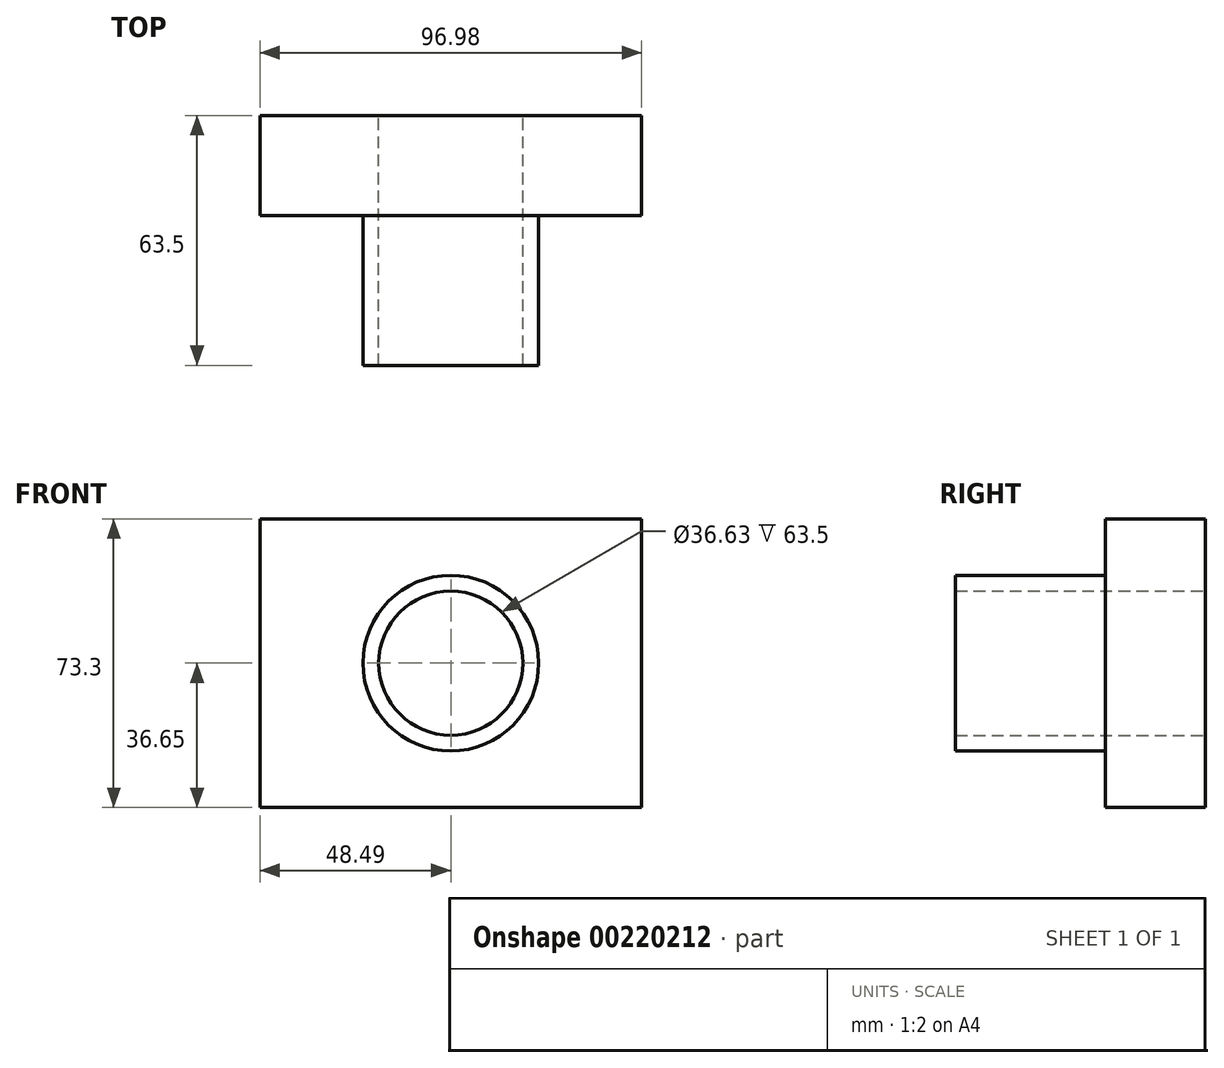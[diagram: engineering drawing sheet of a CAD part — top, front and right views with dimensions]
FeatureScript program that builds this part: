
annotation { "Feature Type Name" : "Feature", "Feature Type Description" : "" }
export const myFeature = defineFeature(function(context is Context, id is Id, definition is map)
    precondition{}
    {
        {
            var Q0;
            Q0=qCreatedBy(makeId("Front.planeOp"),FACE);
            var sketch = newSketch(context, id + "F0", { "sketchPlane" : qUnion([Q0])});
            skLineSegment(sketch, "E0.bottom", {"start": v(-48.5, 36.65) * mm, "end": v(48.5, 36.65) * mm});
            skLineSegment(sketch, "E0.top", {"start": v(-48.5, -36.65) * mm, "end": v(48.5, -36.65) * mm});
            skLineSegment(sketch, "E0.left", {"start": v(-48.5, 36.65) * mm, "end": v(-48.5, -36.65) * mm});
            skLineSegment(sketch, "E0.right", {"start": v(48.5, 36.65) * mm, "end": v(48.5, -36.65) * mm});
            skPoint(sketch, "E0.middle", {"position": v(0, 0) * mm});
            skSolve(sketch);
        }
        {
            var Q0;
            Q0=makeQuery(id+"F0.imprint","IMPRINT",FACE,{"disambiguationData":[TD([[makeQuery(id+"F0.imprint","IMPRINT",EDGE,{"derivedFrom":sQuery(id+"F0.wireOp",EDGE,"E0.bottom")}),-1.0]])]});
            var sketch = newSketch(context, id + "F1", { "sketchPlane" : qUnion([Q0])});
            skCircle(sketch, "E1", {"center": v(0, 0) * mm, "radius": 22.33 * mm});
            skSolve(sketch);
        }
        {
            var Q0;
            Q0=makeQuery(id+"F1.imprint","IMPRINT",FACE,{"disambiguationData":[TD([[makeQuery(id+"F1.imprint","IMPRINT",EDGE,{"derivedFrom":sQuery(id+"F1.wireOp",EDGE,"E1")}),1.0]])]});
            var sketch = newSketch(context, id + "F2", { "sketchPlane" : qUnion([Q0])});
            skCircle(sketch, "E2", {"center": v(0, 0) * mm, "radius": 18.31 * mm});
            skSolve(sketch);
        }
        {
            var Q0;
            Q0 = qSketchRegion(id + "F0", true);
            extrude(context, id + "F3", {"entities" : qUnion([Q0]), "depth" : 25.4 * mm});
        }
        {
            var Q0;
            Q0 = qSketchRegion(id + "F1", true);
            extrude(context, id + "F4", {"entities" : qUnion([Q0]), "operationType" : NewBodyOperationType.ADD, "depth" : 63.5 * mm});
        }
        {
            var Q0;
            Q0 = qSketchRegion(id + "F2", true);
            extrude(context, id + "F5", {"entities" : qUnion([Q0]), "operationType" : NewBodyOperationType.REMOVE, "endBound" : BoundingType.THROUGH_ALL, "depth" : 127 * mm});
        }
    });
